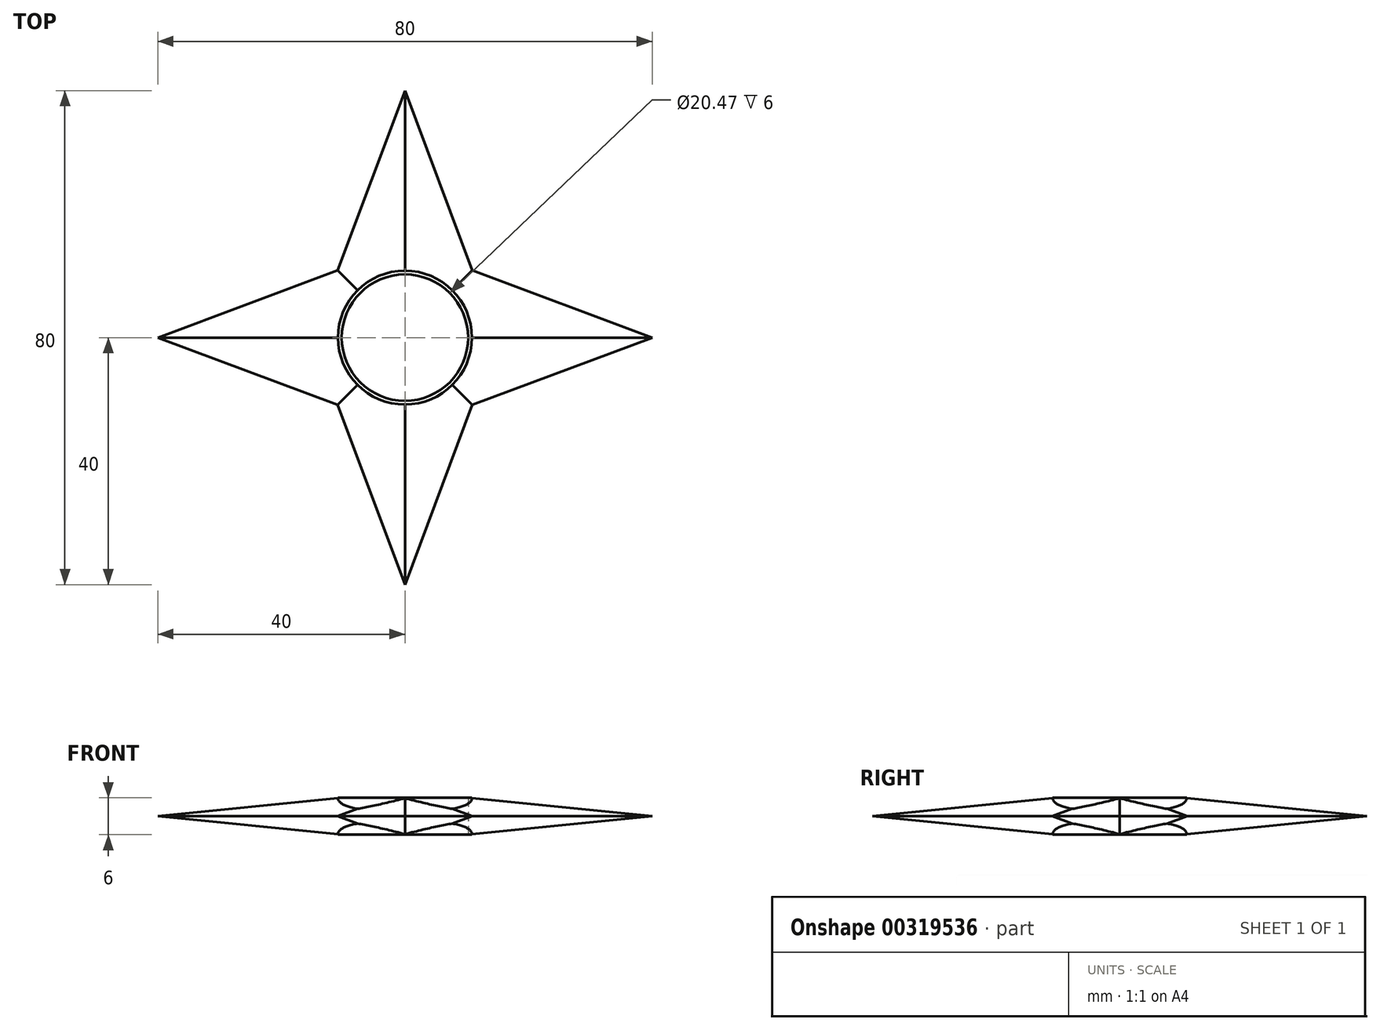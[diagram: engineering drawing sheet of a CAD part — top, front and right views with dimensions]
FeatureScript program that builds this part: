
annotation { "Feature Type Name" : "Feature", "Feature Type Description" : "" }
export const myFeature = defineFeature(function(context is Context, id is Id, definition is map)
    precondition{}
    {
        {
            var Q0;
            Q0=qCreatedBy(makeId("Top.planeOp"),FACE);
            var sketch = newSketch(context, id + "F0", { "sketchPlane" : qUnion([Q0])});
            skCircle(sketch, "E0", {"center": v(0, 0) * mm, "radius": 15 * mm});
            skLineSegment(sketch, "E1", {"start": v(0, 0) * mm, "end": v(0, -6) * mm, "construction": true});
            skLineSegment(sketch, "E2", {"start": v(-15, -6) * mm, "end": v(15, -6) * mm});
            skPoint(sketch, "E3", {"position": v(0, -40) * mm});
            skSolve(sketch);
        }
        {
            var Q0;
            Q0=qCreatedBy(makeId("Front.planeOp"),FACE);
            var sketch = newSketch(context, id + "F1", { "sketchPlane" : qUnion([Q0])});
            skPoint(sketch, "E4.0", {"position": v(-15, 0) * mm});
            skPoint(sketch, "E5.0", {"position": v(15, 0) * mm});
            skLineSegment(sketch, "E6", {"start": v(-15, 0) * mm, "end": v(0, 4) * mm});
            skLineSegment(sketch, "E7", {"start": v(0, 4) * mm, "end": v(15, 0) * mm});
            skLineSegment(sketch, "E8.0", {"start": v(-15, 0) * mm, "end": v(15, 0) * mm});
            skLineSegment(sketch, "E9", {"start": v(0, 0) * mm, "end": v(0, 2.22) * mm, "construction": true});
            skSolve(sketch);
        }
        {
            var Q0;
            Q0=makeQuery(id+"F1.imprint","IMPRINT",FACE,{"disambiguationData":[TD([[makeQuery(id+"F1.imprint","IMPRINT",EDGE,{"derivedFrom":sQuery(id+"F1.wireOp",EDGE,"E6")}),-1.0]])]});
            var Q1;
            Q1=sQuery(id+"F0.wireOp",VERTEX,"E3");
            loft(context, id + "F2", {"sheetProfilesArray" : [{ "sheetProfileEntities" : qUnion([Q0]) }, { "sheetProfileEntities" : qUnion([Q1]) }]});
        }
        {
            var Q0;
            Q0=makeQuery(id+"F2.opLoft","SWEPT_BODY",BODY,{"disambiguationData":[OSD([sQuery(id+"F0.wireOp",VERTEX,"E3"),makeQuery(id+"F1.imprint","IMPRINT",FACE,{"disambiguationData":[TD([[makeQuery(id+"F1.imprint","IMPRINT",EDGE,{"derivedFrom":sQuery(id+"F1.wireOp",EDGE,"E6")}),-1.0]])]})])]});
            var Q1;
            Q1=sQuery(id+"F1.wireOp",EDGE,"E9");
            circularPattern(context, id + "F3", {"operationType" : NewBodyOperationType.ADD, "entities" : qUnion([Q0]), "axis" : qUnion([Q1]), "angle" : 360 * degree, "instanceCount" : 4, "equalSpace" : true});
        }
        {
            var Q0;
            Q0=qCreatedBy(makeId("Top.planeOp"),FACE);
            var sketch = newSketch(context, id + "F4", { "sketchPlane" : qUnion([Q0])});
            skCircle(sketch, "E10", {"center": v(0, 0) * mm, "radius": 10.23 * mm});
            skSolve(sketch);
        }
        {
            var Q0;
            Q0 = qSketchRegion(id + "F4", true);
            extrude(context, id + "F5", {"entities" : qUnion([Q0]), "operationType" : NewBodyOperationType.REMOVE, "depth" : 25 * mm});
        }
        {
            var Q0;
            Q0=qCreatedBy(makeId("Top.planeOp"),FACE);
            var sketch = newSketch(context, id + "F6", { "sketchPlane" : qUnion([Q0])});
            skCircle(sketch, "E11", {"center": v(0, 0) * mm, "radius": 10.83 * mm});
            skCircle(sketch, "E12.0", {"center": v(0, 0) * mm, "radius": 10.23 * mm});
            skSolve(sketch);
        }
        {
            var Q0;
            Q0 = qSketchRegion(id + "F6", true);
            extrude(context, id + "F7", {"entities" : qUnion([Q0]), "operationType" : NewBodyOperationType.ADD, "depth" : 3 * mm});
        }
        {
            var Q0;
            Q0=makeQuery(id+"F2.opLoft","SWEPT_BODY",BODY,{"disambiguationData":[OSD([sQuery(id+"F0.wireOp",VERTEX,"E3"),makeQuery(id+"F1.imprint","IMPRINT",FACE,{"disambiguationData":[TD([[makeQuery(id+"F1.imprint","IMPRINT",EDGE,{"derivedFrom":sQuery(id+"F1.wireOp",EDGE,"E6")}),-1.0]])]})])]});
            var Q1;
            Q1=qCreatedBy(makeId("Top.planeOp"),FACE);
            mirror(context, id + "F8", {"operationType" : NewBodyOperationType.ADD, "entities" : qUnion([Q0]), "mirrorPlane" : qUnion([Q1])});
        }
    });
